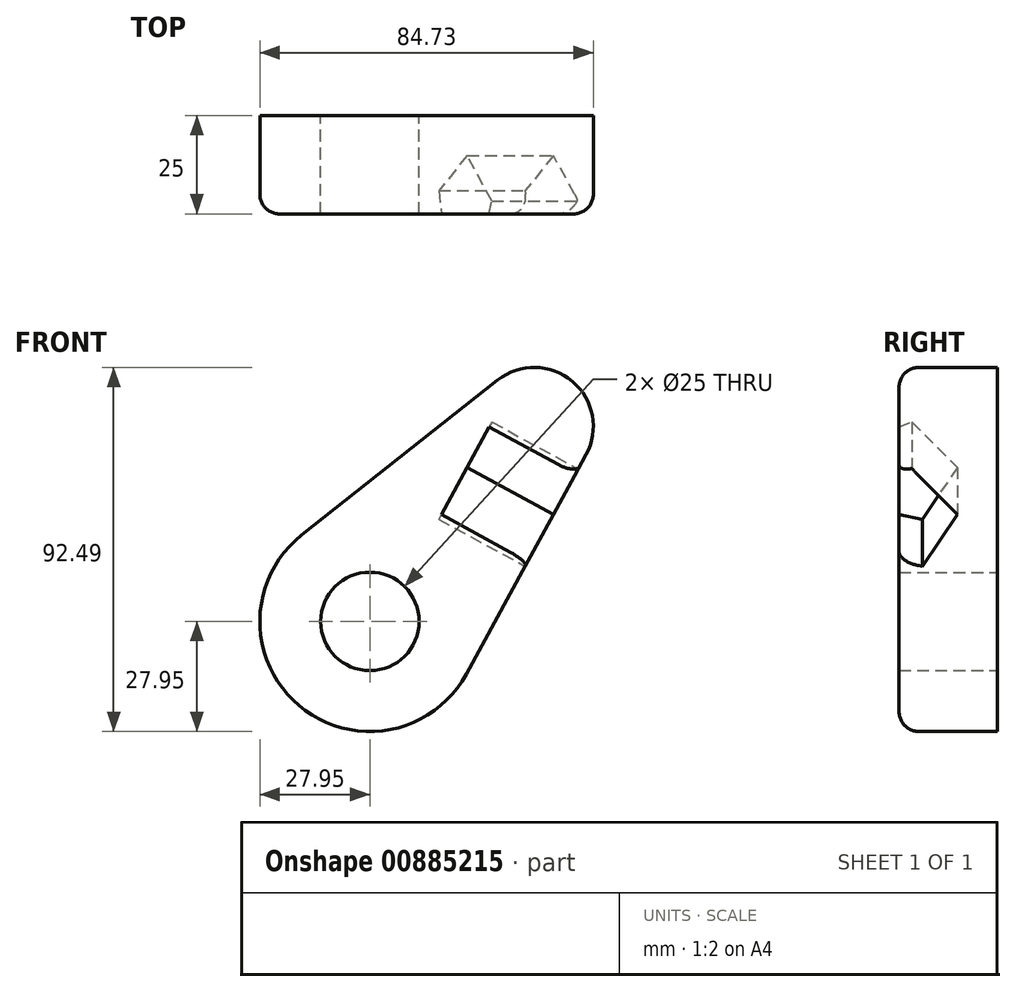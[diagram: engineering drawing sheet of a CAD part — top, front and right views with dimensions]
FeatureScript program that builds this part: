
annotation { "Feature Type Name" : "Feature", "Feature Type Description" : "" }
export const myFeature = defineFeature(function(context is Context, id is Id, definition is map)
    precondition{}
    {
        {
            var Q0;
            Q0=qCreatedBy(makeId("Front.planeOp"),FACE);
            var sketch = newSketch(context, id + "F0", { "sketchPlane" : qUnion([Q0])});
            skCircle(sketch, "E0", {"center": v(0, 0) * mm, "radius": 27.95 * mm});
            skCircle(sketch, "E1", {"center": v(0, 0) * mm, "radius": 12.5 * mm});
            skCircle(sketch, "E2", {"center": v(41.78, 49.54) * mm, "radius": 15 * mm});
            skLineSegment(sketch, "E3", {"start": v(-17.33, 21.93) * mm, "end": v(32.48, 61.3) * mm});
            skLineSegment(sketch, "E4", {"start": v(24.53, -13.39) * mm, "end": v(54.95, 42.35) * mm});
            skSolve(sketch);
        }
        {
            var Q0;
            Q0=makeQuery(id+"F0.imprint","IMPRINT",FACE,{"disambiguationData":[TD([[makeQuery(id+"F0.imprint","IMPRINT",EDGE,{"derivedFrom":sQuery(id+"F0.wireOp",EDGE,"E1")}),-1.0]])]});
            var Q1;
            {var subQ0=sQuery(id+"F0.wireOp",EDGE,"E3");Q1=makeQuery(id+"F0.imprint","IMPRINT",FACE,{"disambiguationData":[TD([[makeQuery(id+"F0.imprint","IMPRINT",EDGE,{"derivedFrom":subQ0}),-1.0]])]});}
            var Q2;
            {var subQ0=sQuery(id+"F0.wireOp",EDGE,"E2");var subQ1=makeQuery(id+"F0.imprint","INTERSECT",VERTEX,{"derivedFrom":[subQ0,sQuery(id+"F0.wireOp",EDGE,"E3")]});Q2=makeQuery(id+"F0.imprint","IMPRINT",FACE,{"disambiguationData":[TD([[makeQuery(id+"F0.imprint","IMPRINT",EDGE,{"disambiguationData":[TD([[subQ1,-1.0]])],"derivedFrom":subQ0}),1.0]])]});}
            extrude(context, id + "F1", {"entities" : qUnion([Q0, Q1, Q2]), "depth" : 25 * mm, "offsetDistance" : 25 * mm});
        }
        {
            var Q0;
            Q0=makeQuery(id+"F1.opExtrude","SWEPT_FACE",FACE,{"disambiguationData":[OSD([sQuery(id+"F0.wireOp",EDGE,"E4")])]});
            var sketch = newSketch(context, id + "F2", { "sketchPlane" : qUnion([Q0])});
            skCircle(sketch, "E5.cCircle", {"center": v(-25, 44.83) * mm, "radius": 12.03 * mm, "construction": true});
            skLineSegment(sketch, "E5.0", {"start": v(-10.2, 46.2) * mm, "end": v(-19.13, 31.18) * mm});
            skLineSegment(sketch, "E5.1", {"start": v(-19.13, 31.18) * mm, "end": v(-36.17, 35.03) * mm});
            skLineSegment(sketch, "E5.2", {"start": v(-36.17, 35.03) * mm, "end": v(-37.78, 52.43) * mm});
            skLineSegment(sketch, "E5.3", {"start": v(-37.78, 52.43) * mm, "end": v(-21.72, 59.33) * mm});
            skLineSegment(sketch, "E5.4", {"start": v(-21.72, 59.33) * mm, "end": v(-10.2, 46.2) * mm});
            skPoint(sketch, "E5.0.midPoint", {"position": v(-14.66, 38.69) * mm});
            skSolve(sketch);
        }
        {
            var Q0;
            {var subQ2=sQuery(id+"F2.wireOp",EDGE,"E5.0");Q0=makeQuery(id+"F2.imprint","IMPRINT",FACE,{"disambiguationData":[TD([[makeQuery(id+"F2.imprint","IMPRINT",EDGE,{"derivedFrom":subQ2}),-1.0]])]});}
            extrude(context, id + "F3", {"entities" : qUnion([Q0]), "operationType" : NewBodyOperationType.REMOVE, "oppositeDirection" : true, "depth" : 25 * mm, "offsetDistance" : 25 * mm});
        }
        {
            var Q0;
            Q0=makeQuery(id+"F1.opExtrude","CAP_EDGE",EDGE,{"disambiguationData":[OSD([sQuery(id+"F0.wireOp",EDGE,"E3")])],"isStart":false});
            fillet(context, id + "F4", {"entities" : qUnion([Q0]), "radius" : 5 * mm, "tangentPropagation" : true, "allowEdgeOverflow" : false});
        }
    });
